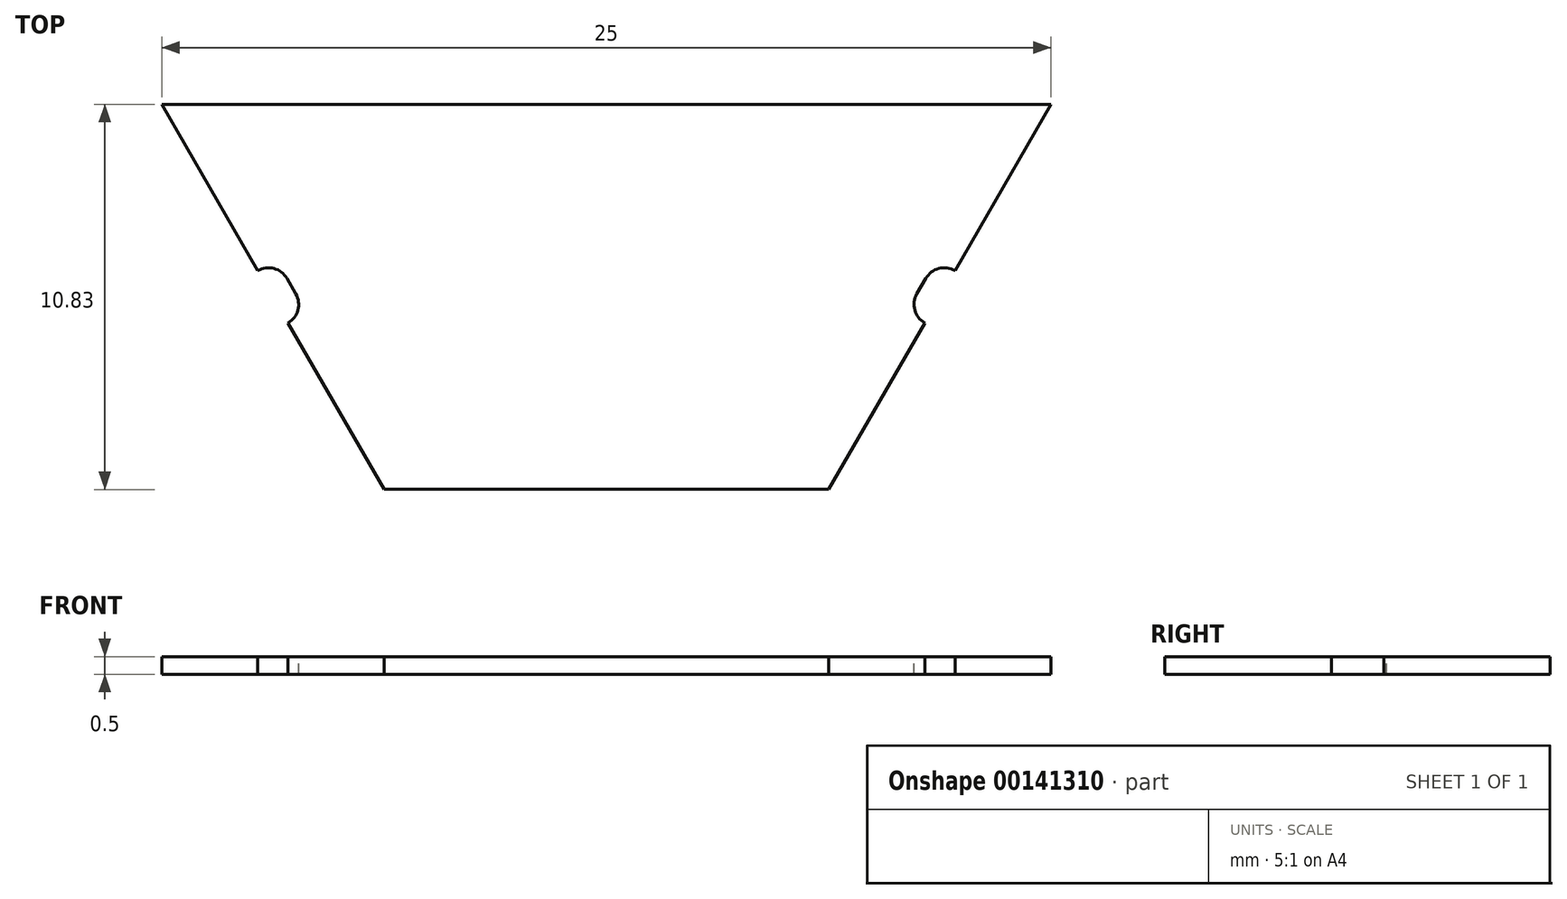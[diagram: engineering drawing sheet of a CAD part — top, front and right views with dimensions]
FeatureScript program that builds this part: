
annotation { "Feature Type Name" : "Feature", "Feature Type Description" : "" }
export const myFeature = defineFeature(function(context is Context, id is Id, definition is map)
    precondition{}
    {
        {
            var Q0;
            Q0=qCreatedBy(makeId("Top.planeOp"),FACE);
            var sketch = newSketch(context, id + "F0", { "sketchPlane" : qUnion([Q0])});
            skCircle(sketch, "E0.cCircle", {"center": v(0, 0) * mm, "radius": 12.5 * mm, "construction": true});
            skLineSegment(sketch, "E0.0", {"start": v(12.5, 0) * mm, "end": v(6.25, -10.83) * mm});
            skLineSegment(sketch, "E0.1", {"start": v(6.25, -10.83) * mm, "end": v(-6.25, -10.83) * mm});
            skLineSegment(sketch, "E0.2", {"start": v(-6.25, -10.83) * mm, "end": v(-12.5, 0) * mm});
            skLineSegment(sketch, "E0.3", {"start": v(-12.5, 0) * mm, "end": v(-6.25, 10.83) * mm});
            skLineSegment(sketch, "E0.4", {"start": v(-6.25, 10.83) * mm, "end": v(6.25, 10.83) * mm});
            skLineSegment(sketch, "E0.5", {"start": v(6.25, 10.83) * mm, "end": v(12.5, 0) * mm});
            skSolve(sketch);
        }
        {
            var Q0;
            Q0=qSketchRegion(id+"F0",true);
            extrude(context, id + "F1", {"entities" : qUnion([Q0]), "depth" : 0.5 * mm});
        }
        {
            var Q0;
            Q0=makeQuery(id+"F1.opExtrude","CAP_FACE",FACE,{"disambiguationData":[OSD([sQuery(id+"F0.wireOp",EDGE,"E0.0"),sQuery(id+"F0.wireOp",EDGE,"E0.1"),sQuery(id+"F0.wireOp",EDGE,"E0.2"),sQuery(id+"F0.wireOp",EDGE,"E0.3"),sQuery(id+"F0.wireOp",EDGE,"E0.4"),sQuery(id+"F0.wireOp",EDGE,"E0.5")])],"isStart":false});
            var sketch = newSketch(context, id + "F2", { "sketchPlane" : qUnion([Q0])});
            skLineSegment(sketch, "E1.0", {"start": v(6.25, -10.83) * mm, "end": v(-6.25, -10.83) * mm, "construction": true});
            skLineSegment(sketch, "E2", {"start": v(0.25, -10.23) * mm, "end": v(-0.25, -10.23) * mm});
            skArc(sketch, "E3", {"start": v(-0.25, -10.23) * mm, "mid": v(-0.67, -10.4) * mm, "end": v(-0.85, -10.83) * mm});
            skArc(sketch, "E4", {"start": v(0.85, -10.83) * mm, "mid": v(0.67, -10.4) * mm, "end": v(0.25, -10.23) * mm});
            skLineSegment(sketch, "E5", {"start": v(-0.85, -10.83) * mm, "end": v(0.85, -10.83) * mm});
            skArc(sketch, "E6.1.0", {"start": v(8.98, 4.9) * mm, "mid": v(9.34, 4.62) * mm, "end": v(9.8, 4.68) * mm});
            skLineSegment(sketch, "E6.1.1", {"start": v(9.8, 4.68) * mm, "end": v(8.95, 6.15) * mm});
            skLineSegment(sketch, "E6.1.2", {"start": v(8.73, 5.33) * mm, "end": v(8.98, 4.9) * mm});
            skArc(sketch, "E6.1.3", {"start": v(8.95, 6.15) * mm, "mid": v(8.67, 5.78) * mm, "end": v(8.73, 5.33) * mm});
            skArc(sketch, "E6.2.0", {"start": v(-8.73, 5.33) * mm, "mid": v(-8.67, 5.78) * mm, "end": v(-8.95, 6.15) * mm});
            skLineSegment(sketch, "E6.2.1", {"start": v(-8.95, 6.15) * mm, "end": v(-9.8, 4.68) * mm});
            skLineSegment(sketch, "E6.2.2", {"start": v(-8.98, 4.9) * mm, "end": v(-8.73, 5.33) * mm});
            skArc(sketch, "E6.2.3", {"start": v(-9.8, 4.68) * mm, "mid": v(-9.34, 4.62) * mm, "end": v(-8.98, 4.9) * mm});
            skPoint(sketch, "E6.center", {"position": v(0, 0) * mm});
            skSolve(sketch);
        }
        {
            var Q0;
            Q0=qSketchRegion(id+"F2",true);
            extrude(context, id + "F3", {"entities" : qUnion([Q0]), "operationType" : NewBodyOperationType.REMOVE, "endBound" : BoundingType.THROUGH_ALL, "oppositeDirection" : true, "depth" : 25 * mm});
        }
        {
            var Q0;
            Q0=makeQuery(id+"F1.opExtrude","CAP_FACE",FACE,{"disambiguationData":[OSD([sQuery(id+"F0.wireOp",EDGE,"E0.0"),sQuery(id+"F0.wireOp",EDGE,"E0.1"),sQuery(id+"F0.wireOp",EDGE,"E0.2"),sQuery(id+"F0.wireOp",EDGE,"E0.3"),sQuery(id+"F0.wireOp",EDGE,"E0.4"),sQuery(id+"F0.wireOp",EDGE,"E0.5")])],"isStart":false});
            var sketch = newSketch(context, id + "F4", { "sketchPlane" : qUnion([Q0])});
            skLineSegment(sketch, "E7", {"start": v(-12.5, 0) * mm, "end": v(12.5, 0) * mm});
            skLineSegment(sketch, "E8", {"start": v(12.5, 0) * mm, "end": v(6.25, -10.83) * mm});
            skLineSegment(sketch, "E9", {"start": v(6.25, -10.83) * mm, "end": v(-6.25, -10.83) * mm});
            skLineSegment(sketch, "E10", {"start": v(-6.25, -10.83) * mm, "end": v(-12.5, 0) * mm});
            skSolve(sketch);
        }
        {
            var Q0;
            Q0 = qSketchRegion(id + "F4", true);
            extrude(context, id + "F5", {"entities" : qUnion([Q0]), "operationType" : NewBodyOperationType.REMOVE, "endBound" : BoundingType.THROUGH_ALL, "oppositeDirection" : true, "depth" : 25 * mm});
        }
        {
            var Q0;
            Q0=qCreatedBy(makeId("Right.planeOp"),FACE);
            var sketch = newSketch(context, id + "F6", { "sketchPlane" : qUnion([Q0])});
            skLineSegment(sketch, "E11", {"start": v(0, 0) * mm, "end": v(0, 10.96) * mm, "construction": true});
            skSolve(sketch);
        }
        {
            var Q0;
            Q0=makeQuery(id+"F1.opExtrude","SWEPT_BODY",BODY,{"disambiguationData":[OSD([sQuery(id+"F0.wireOp",EDGE,"E0.0"),sQuery(id+"F0.wireOp",EDGE,"E0.1"),sQuery(id+"F0.wireOp",EDGE,"E0.2"),sQuery(id+"F0.wireOp",EDGE,"E0.3"),sQuery(id+"F0.wireOp",EDGE,"E0.4"),sQuery(id+"F0.wireOp",EDGE,"E0.5")])]});
            var Q1;
            Q1=sQuery(id+"F6.wireOp",EDGE,"E11");
            transform(context, id + "F7", {"entities" : qUnion([Q0]), "transformType" : TransformType.ROTATION, "transformAxis" : qUnion([Q1]), "angle" : 180 * degree, "makeCopy" : false});
        }
    });
